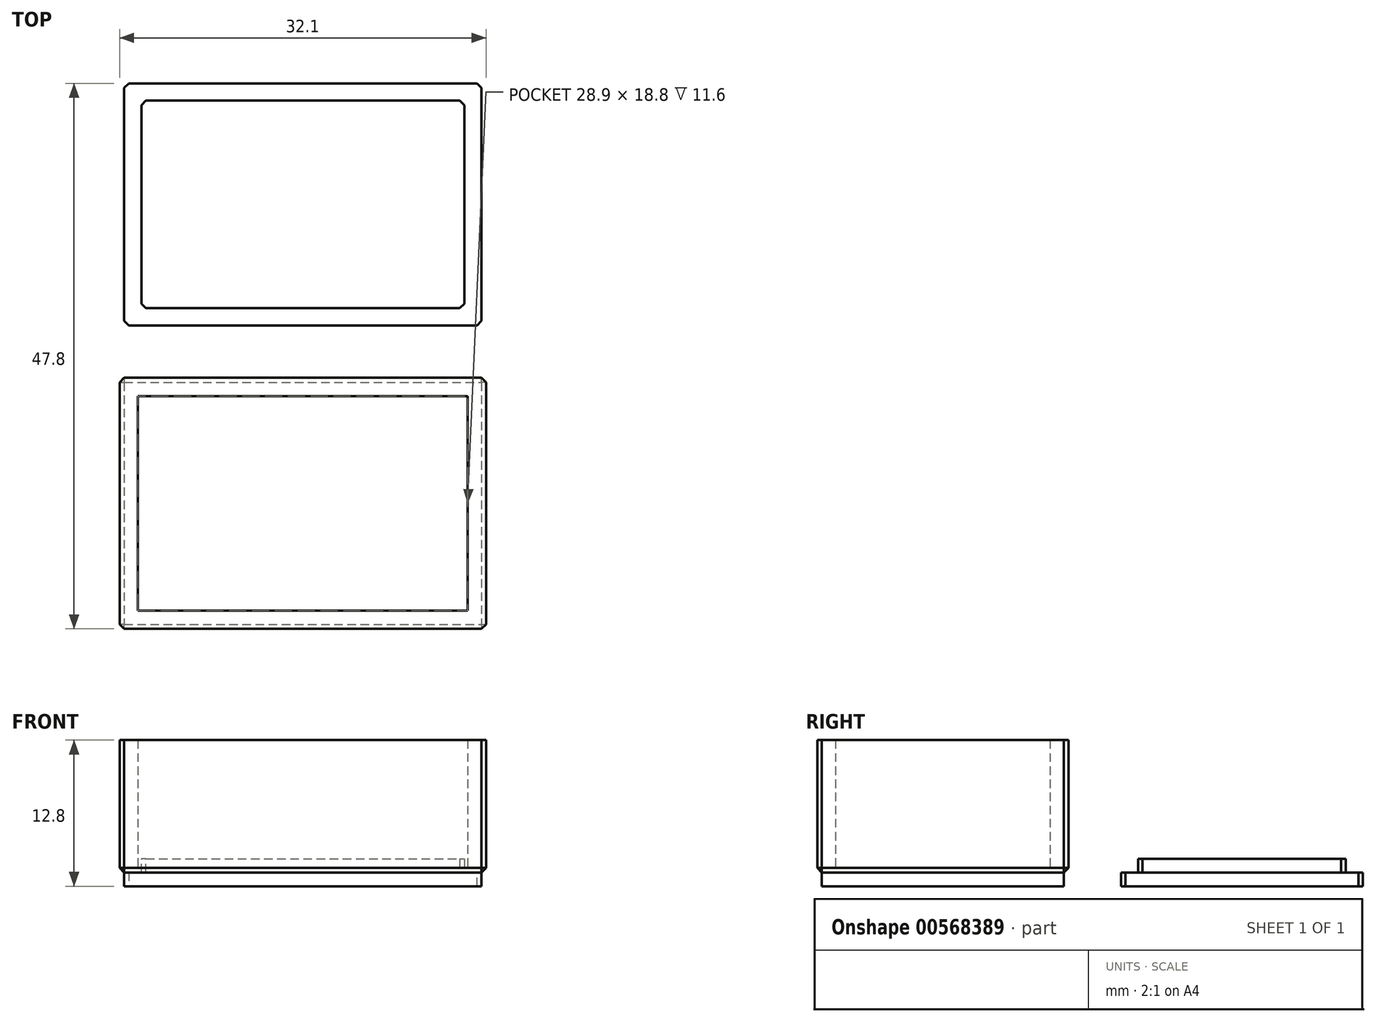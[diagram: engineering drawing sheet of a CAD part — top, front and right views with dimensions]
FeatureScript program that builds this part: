
annotation { "Feature Type Name" : "Feature", "Feature Type Description" : "" }
export const myFeature = defineFeature(function(context is Context, id is Id, definition is map)
    precondition{}
    {
        {
            var Q0;
            Q0=qCreatedBy(makeId("Top.planeOp"),FACE);
            var sketch = newSketch(context, id + "F0", { "sketchPlane" : qUnion([Q0])});
            skLineSegment(sketch, "E0.bottom", {"start": v(-15.65, 10.6) * mm, "end": v(15.65, 10.6) * mm});
            skLineSegment(sketch, "E0.top", {"start": v(-15.65, -10.6) * mm, "end": v(15.65, -10.6) * mm});
            skLineSegment(sketch, "E0.left", {"start": v(-15.65, 10.6) * mm, "end": v(-15.65, -10.6) * mm});
            skLineSegment(sketch, "E0.right", {"start": v(15.65, 10.6) * mm, "end": v(15.65, -10.6) * mm});
            skPoint(sketch, "E0.middle", {"position": v(0, 0) * mm});
            skLineSegment(sketch, "E1.bottom", {"start": v(15.65, 15.6) * mm, "end": v(-15.65, 15.6) * mm});
            skLineSegment(sketch, "E1.top", {"start": v(15.65, 36.8) * mm, "end": v(-15.65, 36.8) * mm});
            skLineSegment(sketch, "E1.left", {"start": v(15.65, 15.6) * mm, "end": v(15.65, 36.8) * mm});
            skLineSegment(sketch, "E1.right", {"start": v(-15.65, 15.6) * mm, "end": v(-15.65, 36.8) * mm});
            skPoint(sketch, "E1.middle", {"position": v(0, 26.2) * mm});
            skSolve(sketch);
        }
        {
            var Q0;
            Q0=qSketchRegion(id+"F0",true);
            extrude(context, id + "F1", {"entities" : qUnion([Q0]), "depth" : 1.2 * mm, "offsetDistance" : 25 * mm});
        }
        {
            var Q0;
            Q0=makeQuery(id+"F1.opExtrude","CAP_FACE",FACE,{"disambiguationData":[OSD([sQuery(id+"F0.wireOp",EDGE,"E0.bottom"),sQuery(id+"F0.wireOp",EDGE,"E0.top"),sQuery(id+"F0.wireOp",EDGE,"E0.left"),sQuery(id+"F0.wireOp",EDGE,"E0.right")])],"isStart":false});
            var sketch = newSketch(context, id + "F2", { "sketchPlane" : qUnion([Q0])});
            skLineSegment(sketch, "E2.bottom", {"start": v(-14.45, 9.4) * mm, "end": v(14.45, 9.4) * mm});
            skLineSegment(sketch, "E2.top", {"start": v(-14.45, -9.4) * mm, "end": v(14.45, -9.4) * mm});
            skLineSegment(sketch, "E2.left", {"start": v(-14.45, 9.4) * mm, "end": v(-14.45, -9.4) * mm});
            skLineSegment(sketch, "E2.right", {"start": v(14.45, 9.4) * mm, "end": v(14.45, -9.4) * mm});
            skPoint(sketch, "E2.middle", {"position": v(0, 0) * mm});
            skLineSegment(sketch, "E3.bottom", {"start": v(-15.65, 10.6) * mm, "end": v(15.65, 10.6) * mm});
            skLineSegment(sketch, "E3.top", {"start": v(-15.65, -10.6) * mm, "end": v(15.65, -10.6) * mm});
            skLineSegment(sketch, "E3.left", {"start": v(-15.65, 10.6) * mm, "end": v(-15.65, -10.6) * mm});
            skLineSegment(sketch, "E3.right", {"start": v(15.65, 10.6) * mm, "end": v(15.65, -10.6) * mm});
            skLineSegment(sketch, "E4.bottom", {"start": v(-16.05, 11) * mm, "end": v(16.05, 11) * mm});
            skLineSegment(sketch, "E4.top", {"start": v(-16.05, -11) * mm, "end": v(16.05, -11) * mm});
            skLineSegment(sketch, "E4.left", {"start": v(-16.05, 11) * mm, "end": v(-16.05, -11) * mm});
            skLineSegment(sketch, "E4.right", {"start": v(16.05, 11) * mm, "end": v(16.05, -11) * mm});
            skSolve(sketch);
        }
        {
            var Q0;
            Q0=makeQuery(id+"F2.imprint","IMPRINT",FACE,{"disambiguationData":[TD([[makeQuery(id+"F2.imprint","IMPRINT",EDGE,{"derivedFrom":sQuery(id+"F2.wireOp",EDGE,"E3.bottom")}),1.0]])]});
            var Q1;
            Q1=makeQuery(id+"F2.imprint","IMPRINT",FACE,{"disambiguationData":[TD([[makeQuery(id+"F2.imprint","IMPRINT",EDGE,{"derivedFrom":sQuery(id+"F2.wireOp",EDGE,"E2.bottom")}),1.0]])]});
            extrude(context, id + "F3", {"entities" : qUnion([Q0, Q1]), "operationType" : NewBodyOperationType.ADD, "depth" : 11.6 * mm, "offsetDistance" : 25 * mm});
        }
        {
            var Q0;
            Q0=makeQuery(id+"F1.opExtrude","CAP_FACE",FACE,{"disambiguationData":[OSD([sQuery(id+"F0.wireOp",EDGE,"E1.bottom"),sQuery(id+"F0.wireOp",EDGE,"E1.top"),sQuery(id+"F0.wireOp",EDGE,"E1.left"),sQuery(id+"F0.wireOp",EDGE,"E1.right")])],"isStart":false});
            var sketch = newSketch(context, id + "F4", { "sketchPlane" : qUnion([Q0])});
            skLineSegment(sketch, "E5.bottom", {"start": v(-14.15, 35.3) * mm, "end": v(14.15, 35.3) * mm});
            skLineSegment(sketch, "E5.top", {"start": v(-14.15, 17.1) * mm, "end": v(14.15, 17.1) * mm});
            skLineSegment(sketch, "E5.left", {"start": v(-14.15, 35.3) * mm, "end": v(-14.15, 17.1) * mm});
            skLineSegment(sketch, "E5.right", {"start": v(14.15, 35.3) * mm, "end": v(14.15, 17.1) * mm});
            skPoint(sketch, "E5.middle", {"position": v(0, 26.2) * mm});
            skSolve(sketch);
        }
        {
            var Q0;
            Q0=makeQuery(id+"F4.imprint","IMPRINT",FACE,{"disambiguationData":[TD([[makeQuery(id+"F4.imprint","IMPRINT",EDGE,{"derivedFrom":sQuery(id+"F4.wireOp",EDGE,"E5.bottom")}),-1.0]])]});
            extrude(context, id + "F5", {"entities" : qUnion([Q0]), "operationType" : NewBodyOperationType.ADD, "depth" : 1.2 * mm, "offsetDistance" : 25 * mm});
        }
        {
            var Q0;
            Q0=makeQuery(id+"F3.opExtrude","CAP_EDGE",EDGE,{"disambiguationData":[OSD([sQuery(id+"F2.wireOp",EDGE,"E4.left")])],"isStart":true});
            var Q1;
            Q1=makeQuery(id+"F3.opExtrude","CAP_EDGE",EDGE,{"disambiguationData":[OSD([sQuery(id+"F2.wireOp",EDGE,"E4.top")])],"isStart":true});
            var Q2;
            Q2=makeQuery(id+"F3.opExtrude","CAP_EDGE",EDGE,{"disambiguationData":[OSD([sQuery(id+"F2.wireOp",EDGE,"E4.right")])],"isStart":true});
            var Q3;
            Q3=makeQuery(id+"F3.opExtrude","CAP_EDGE",EDGE,{"disambiguationData":[OSD([sQuery(id+"F2.wireOp",EDGE,"E4.bottom")])],"isStart":true});
            var Q4;
            Q4=makeQuery(id+"F3.opExtrude","SWEPT_EDGE",EDGE,{"disambiguationData":[OSD([sQuery(id+"F2.wireOp",EDGE,"E4.top"),sQuery(id+"F2.wireOp",EDGE,"E4.left")])]});
            var Q5;
            Q5=makeQuery(id+"F3.opExtrude","SWEPT_EDGE",EDGE,{"disambiguationData":[OSD([sQuery(id+"F2.wireOp",EDGE,"E4.top"),sQuery(id+"F2.wireOp",EDGE,"E4.right")])]});
            var Q6;
            Q6=makeQuery(id+"F3.opExtrude","SWEPT_EDGE",EDGE,{"disambiguationData":[OSD([sQuery(id+"F2.wireOp",EDGE,"E4.bottom"),sQuery(id+"F2.wireOp",EDGE,"E4.right")])]});
            var Q7;
            Q7=makeQuery(id+"F3.opExtrude","SWEPT_EDGE",EDGE,{"disambiguationData":[OSD([sQuery(id+"F2.wireOp",EDGE,"E4.bottom"),sQuery(id+"F2.wireOp",EDGE,"E4.left")])]});
            var Q8;
            Q8=makeQuery(id+"F1.opExtrude","SWEPT_EDGE",EDGE,{"disambiguationData":[OSD([sQuery(id+"F0.wireOp",EDGE,"E1.top"),sQuery(id+"F0.wireOp",EDGE,"E1.left")])]});
            var Q9;
            Q9=makeQuery(id+"F1.opExtrude","SWEPT_EDGE",EDGE,{"disambiguationData":[OSD([sQuery(id+"F0.wireOp",EDGE,"E1.bottom"),sQuery(id+"F0.wireOp",EDGE,"E1.left")])]});
            var Q10;
            Q10=makeQuery(id+"F1.opExtrude","SWEPT_EDGE",EDGE,{"disambiguationData":[OSD([sQuery(id+"F0.wireOp",EDGE,"E1.top"),sQuery(id+"F0.wireOp",EDGE,"E1.right")])]});
            var Q11;
            Q11=makeQuery(id+"F5.opExtrude","SWEPT_EDGE",EDGE,{"disambiguationData":[OSD([sQuery(id+"F4.wireOp",EDGE,"E5.bottom"),sQuery(id+"F4.wireOp",EDGE,"E5.left")])]});
            var Q12;
            Q12=makeQuery(id+"F5.opExtrude","SWEPT_EDGE",EDGE,{"disambiguationData":[OSD([sQuery(id+"F4.wireOp",EDGE,"E5.bottom"),sQuery(id+"F4.wireOp",EDGE,"E5.right")])]});
            var Q13;
            Q13=makeQuery(id+"F5.opExtrude","SWEPT_EDGE",EDGE,{"disambiguationData":[OSD([sQuery(id+"F4.wireOp",EDGE,"E5.top"),sQuery(id+"F4.wireOp",EDGE,"E5.right")])]});
            var Q14;
            Q14=makeQuery(id+"F5.opExtrude","SWEPT_EDGE",EDGE,{"disambiguationData":[OSD([sQuery(id+"F4.wireOp",EDGE,"E5.top"),sQuery(id+"F4.wireOp",EDGE,"E5.left")])]});
            var Q15;
            Q15=makeQuery(id+"F1.opExtrude","SWEPT_EDGE",EDGE,{"disambiguationData":[OSD([sQuery(id+"F0.wireOp",EDGE,"E1.bottom"),sQuery(id+"F0.wireOp",EDGE,"E1.right")])]});
            chamfer(context, id + "F6", {"entities" : qUnion([Q0, Q1, Q2, Q3, Q4, Q5, Q6, Q7, Q8, Q9, Q10, Q11, Q12, Q13, Q14, Q15]), "width" : .4 * mm, "tangentPropagation" : true});
        }
    });
